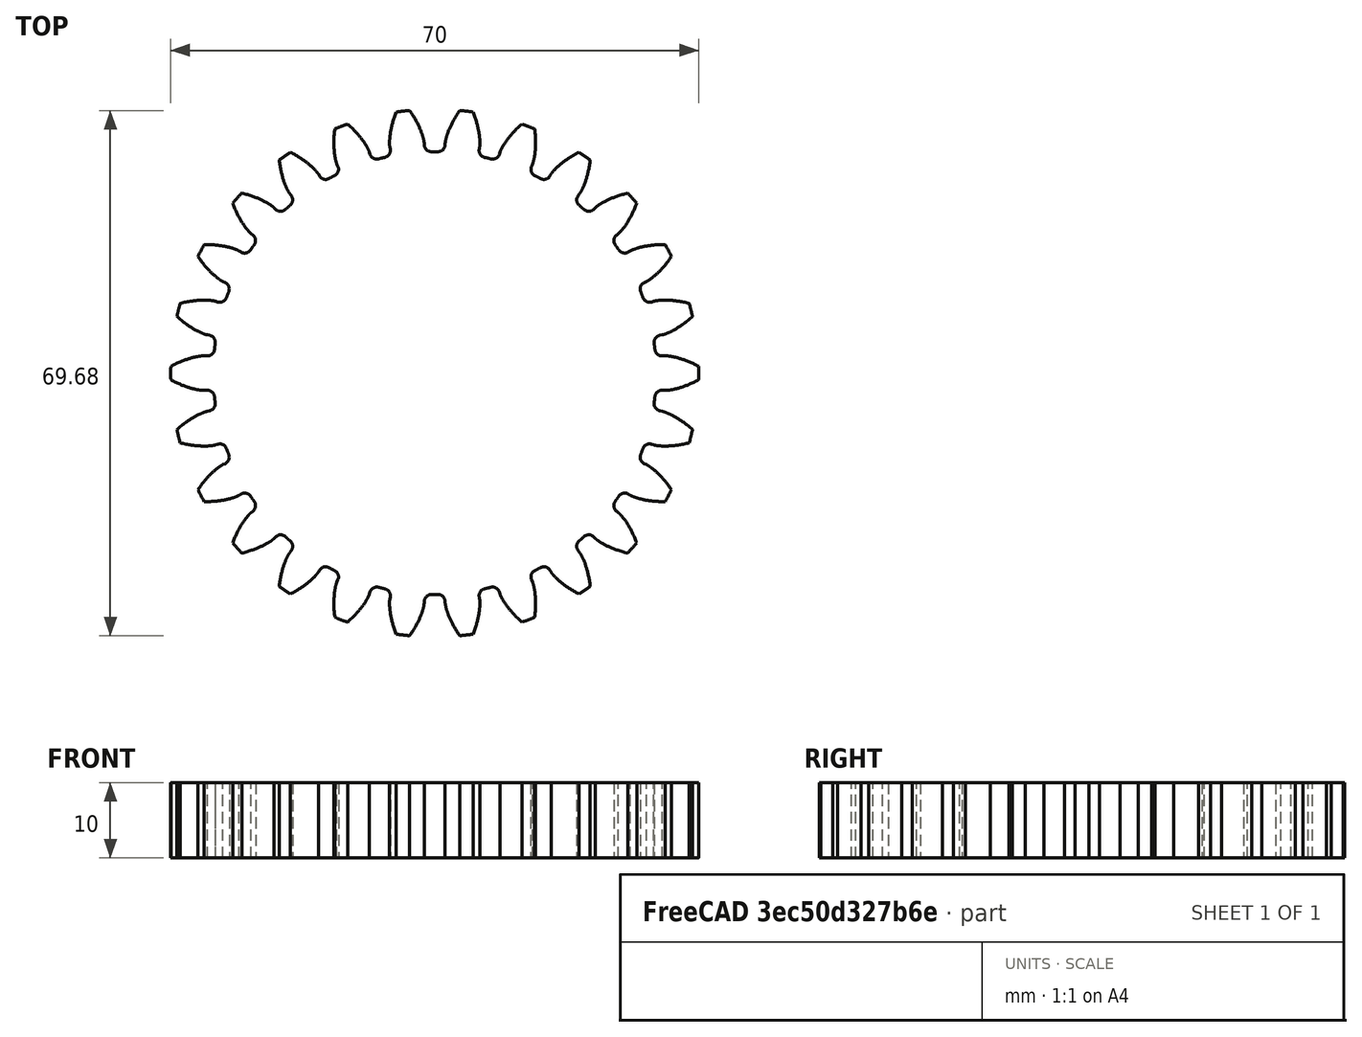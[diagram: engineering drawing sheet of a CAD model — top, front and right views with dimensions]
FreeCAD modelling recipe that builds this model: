
FCSTD DOCUMENT  (FreeCAD 0.19R21300 +2313 (Git))
Label: test
License: All rights reserved
LicenseURL: http://en.wikipedia.org/wiki/All_rights_reserved
objects: App::FeaturePython×2, Part::FeaturePython×2, Part::Part2DObjectPython×1, PartDesign::Pad×1, PartDesign::Body×1
note: 6 computed .brp shape members not serialized (recipe doc carries the construction recipe); baked Part::Feature solids carry a one-line shape summary decoded from their .brp

FEATURE [App::FeaturePython] Constraints  # WARN: FeaturePython — macro-defined, semantics opaque (R4)
  _Version = 1
FEATURE [App::FeaturePython] Elements  # WARN: FeaturePython — macro-defined, semantics opaque (R4)
FEATURE [Part::Part2DObjectPython] InvoluteGear  # Draft 2D object (typed FeaturePython)
  ExternalGear = true
  HighPrecision = true
  Modules = 2.5
  NumberOfTeeth = 26
  PressureAngle = 20
FEATURE [PartDesign::Pad] Pad
  ClaimChildren = false
  Length = 10
  Length2 = 100
  Profile = -> InvoluteGear
  Suppress = false
  Type = 0
FEATURE [PartDesign::Body] Body
  ExportMode = 0
  Group = -> [InvoluteGear,Pad]
  Origin = -> Origin
  Tip = -> Pad
  _ExportChildren = -> [Pad]
  _GroupVersion = 1
FEATURE [Part::FeaturePython] Parts  # WARN: FeaturePython — macro-defined, semantics opaque (R4)
  Group = -> [Body]
  GroupMode = 0
FEATURE [Part::FeaturePython] Assembly  label="test"  # WARN: FeaturePython — macro-defined, semantics opaque (R4)
  AutoRelax = true
  BuildShape = 0
  Freeze = false
  Group = -> [Constraints,Elements,Parts]
  Verbose = false
  _SolverType = 1
  _Version = 1
